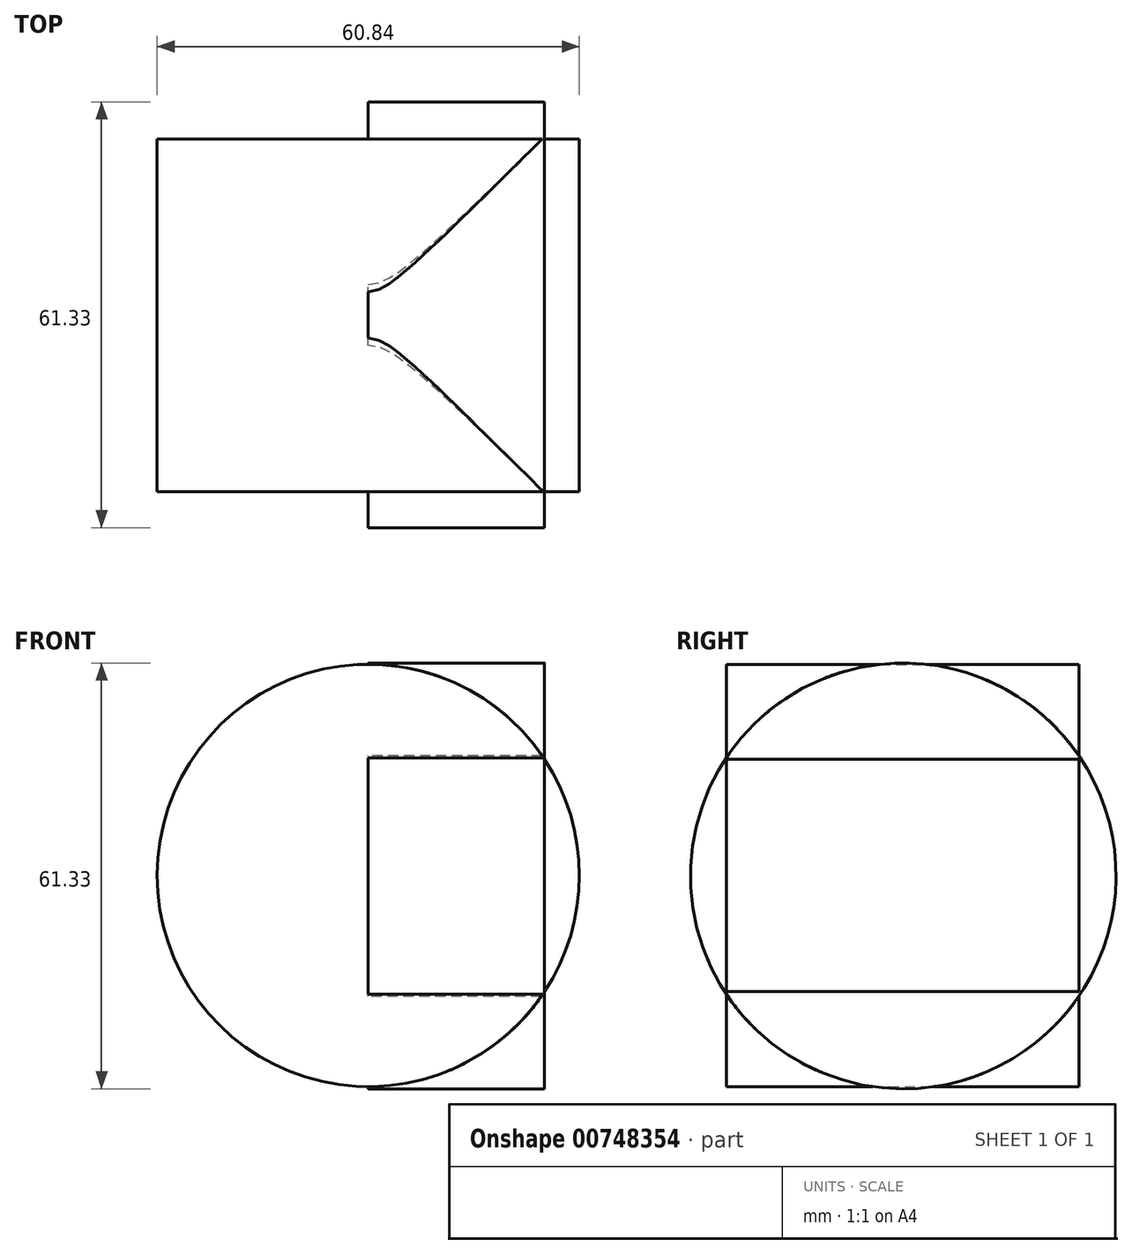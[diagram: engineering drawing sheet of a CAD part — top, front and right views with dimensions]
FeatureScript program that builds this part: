
annotation { "Feature Type Name" : "Feature", "Feature Type Description" : "" }
export const myFeature = defineFeature(function(context is Context, id is Id, definition is map)
    precondition{}
    {
        {
            var Q0;
            Q0=qCreatedBy(makeId("Front.planeOp"),FACE);
            var sketch = newSketch(context, id + "F0", { "sketchPlane" : qUnion([Q0])});
            skCircle(sketch, "E0", {"center": v(0, 0) * mm, "radius": 30.42 * mm});
            skSolve(sketch);
        }
        {
            var Q0;
            Q0=qCreatedBy(makeId("Right.planeOp"),FACE);
            var sketch = newSketch(context, id + "F1", { "sketchPlane" : qUnion([Q0])});
            skCircle(sketch, "E1", {"center": v(0.1, -0.07) * mm, "radius": 30.66 * mm});
            skSolve(sketch);
        }
        {
            var Q0;
            Q0=makeQuery(id+"F0.imprint","IMPRINT",FACE,{"disambiguationData":[TD([[makeQuery(id+"F0.imprint","IMPRINT",EDGE,{"derivedFrom":sQuery(id+"F0.wireOp",EDGE,"E0")}),1.0]])]});
            extrude(context, id + "F2", {"entities" : qUnion([Q0]), "depth" : 25.4 * mm, "offsetDistance" : 25.4 * mm});
        }
        {
            var Q0;
            Q0=makeQuery(id+"F2.opExtrude","CAP_FACE",FACE,{"disambiguationData":[OSD([sQuery(id+"F0.wireOp",EDGE,"E0")])],"isStart":true});
            extrude(context, id + "F3", {"entities" : qUnion([Q0]), "operationType" : NewBodyOperationType.ADD, "depth" : 25.4 * mm, "offsetDistance" : 25.4 * mm});
        }
        {
            var Q0;
            Q0=makeQuery(id+"F1.imprint","IMPRINT",FACE,{"disambiguationData":[TD([[makeQuery(id+"F1.imprint","IMPRINT",EDGE,{"derivedFrom":sQuery(id+"F1.wireOp",EDGE,"E1")}),1.0]])]});
            extrude(context, id + "F4", {"entities" : qUnion([Q0]), "operationType" : NewBodyOperationType.ADD, "depth" : 25.4 * mm, "offsetDistance" : 25.4 * mm});
        }
    });
